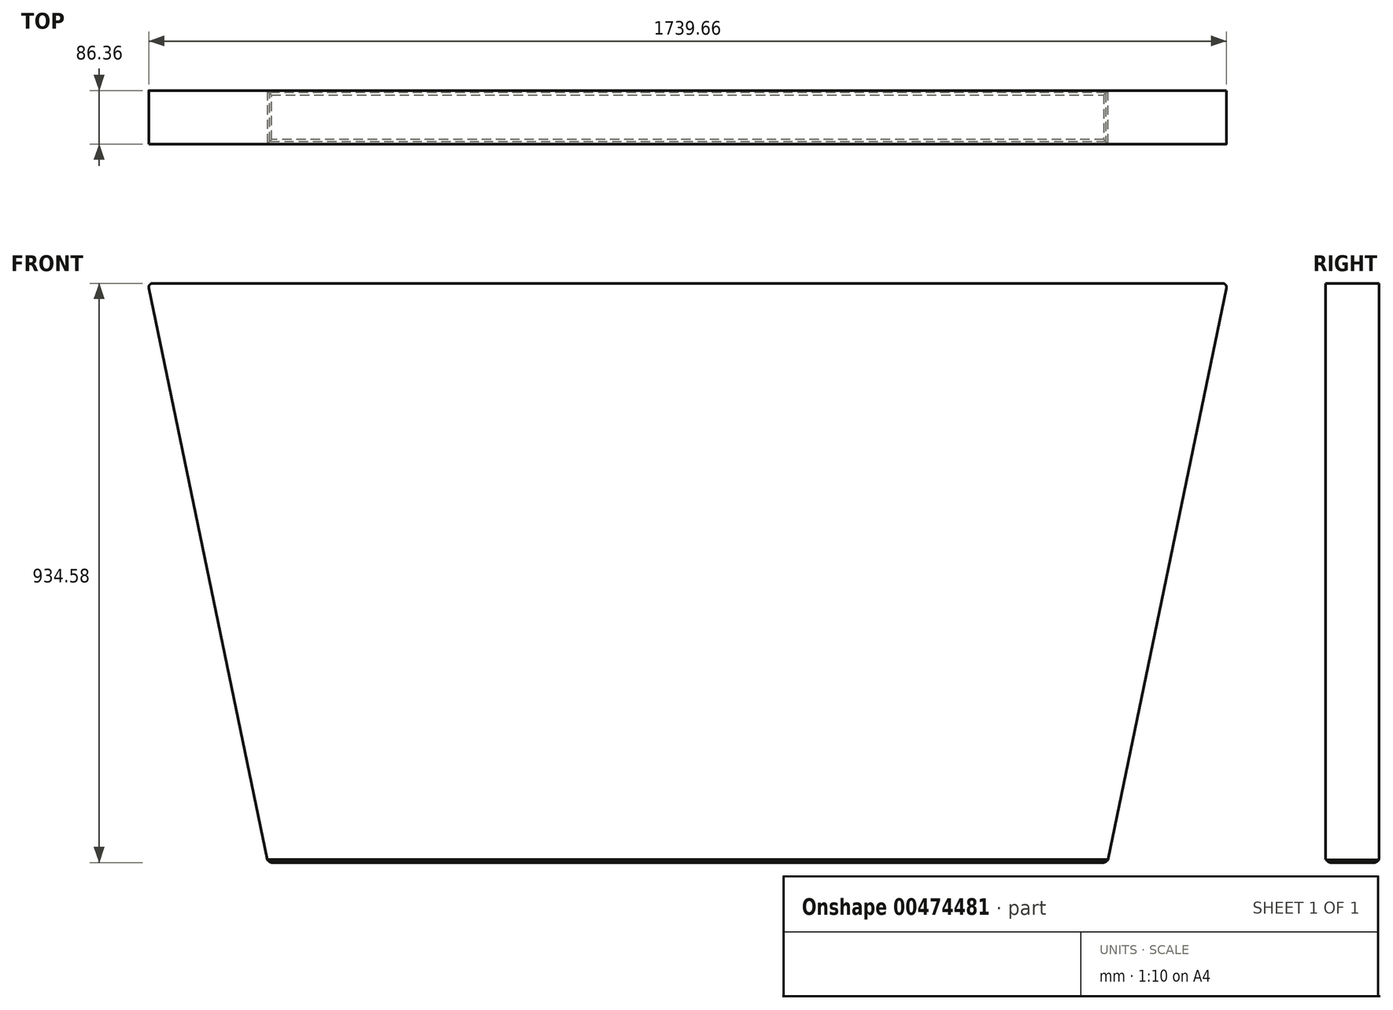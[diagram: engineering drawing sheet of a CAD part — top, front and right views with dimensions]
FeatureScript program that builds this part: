
annotation { "Feature Type Name" : "Feature", "Feature Type Description" : "" }
export const myFeature = defineFeature(function(context is Context, id is Id, definition is map)
    precondition{}
    {
        {
            var Q0;
            Q0=qCreatedBy(makeId("Front.planeOp"),FACE);
            var sketch = newSketch(context, id + "F0", { "sketchPlane" : qUnion([Q0])});
            skLineSegment(sketch, "E0", {"start": v(-1027.3, 476.6) * mm, "end": v(699.65, 476.6) * mm});
            skLineSegment(sketch, "E1", {"start": v(705.86, 468.96) * mm, "end": v(513.83, -457.98) * mm});
            skLineSegment(sketch, "E2", {"start": v(513.83, -457.98) * mm, "end": v(-841.49, -457.98) * mm});
            skLineSegment(sketch, "E3", {"start": v(-841.49, -457.98) * mm, "end": v(-1033.52, 468.96) * mm});
            skPoint(sketch, "E4.visualSharp", {"position": v(-1035.1, 476.6) * mm});
            skArc(sketch, "E4.filletArc", {"start": v(-1027.3, 476.6) * mm, "mid": v(-1032.23, 474.25) * mm, "end": v(-1033.52, 468.96) * mm});
            skPoint(sketch, "E5.visualSharp", {"position": v(707.45, 476.6) * mm});
            skArc(sketch, "E5.filletArc", {"start": v(705.86, 468.96) * mm, "mid": v(704.57, 474.25) * mm, "end": v(699.65, 476.6) * mm});
            skSolve(sketch);
        }
        {
            var Q0;
            Q0 = qSketchRegion(id + "F0", true);
            extrude(context, id + "F1", {"entities" : qUnion([Q0]), "depth" : 86.36 * mm});
        }
        {
            var Q0;
            Q0=makeQuery(id+"F1.opExtrude","CAP_EDGE",EDGE,{"disambiguationData":[OSD([sQuery(id+"F0.wireOp",EDGE,"E2")])],"isStart":true});
            var Q1;
            Q1=makeQuery(id+"F1.opExtrude","SWEPT_FACE",FACE,{"disambiguationData":[OSD([sQuery(id+"F0.wireOp",EDGE,"E2")])]});
            var Q2;
            Q2=makeQuery(id+"F1.opExtrude","SWEPT_EDGE",EDGE,{"disambiguationData":[OSD([sQuery(id+"F0.wireOp",EDGE,"E2"),sQuery(id+"F0.wireOp",EDGE,"E3")])]});
            var Q3;
            Q3=makeQuery(id+"F1.opExtrude","SWEPT_EDGE",EDGE,{"disambiguationData":[OSD([sQuery(id+"F0.wireOp",EDGE,"E1"),sQuery(id+"F0.wireOp",EDGE,"E2")])]});
            var Q4;
            Q4=makeQuery(id+"F1.opExtrude","CAP_EDGE",EDGE,{"disambiguationData":[OSD([sQuery(id+"F0.wireOp",EDGE,"E2")])],"isStart":false});
            chamfer(context, id + "F2", {"entities" : qUnion([Q0, Q1, Q2, Q3, Q4]), "width" : 5.08 * mm, "tangentPropagation" : true});
        }
        {
            var Q0;
            Q0=makeQuery(id+"F1.opExtrude","SWEPT_FACE",FACE,{"disambiguationData":[OSD([sQuery(id+"F0.wireOp",EDGE,"E2")])]});
            var Q1;
            Q1=makeQuery(id+"F1.opExtrude","CAP_EDGE",EDGE,{"disambiguationData":[OSD([sQuery(id+"F0.wireOp",EDGE,"E2")])],"isStart":false});
            chamfer(context, id + "F3", {"entities" : qUnion([Q0, Q1]), "width" : 5.08 * mm, "tangentPropagation" : true});
        }
    });
